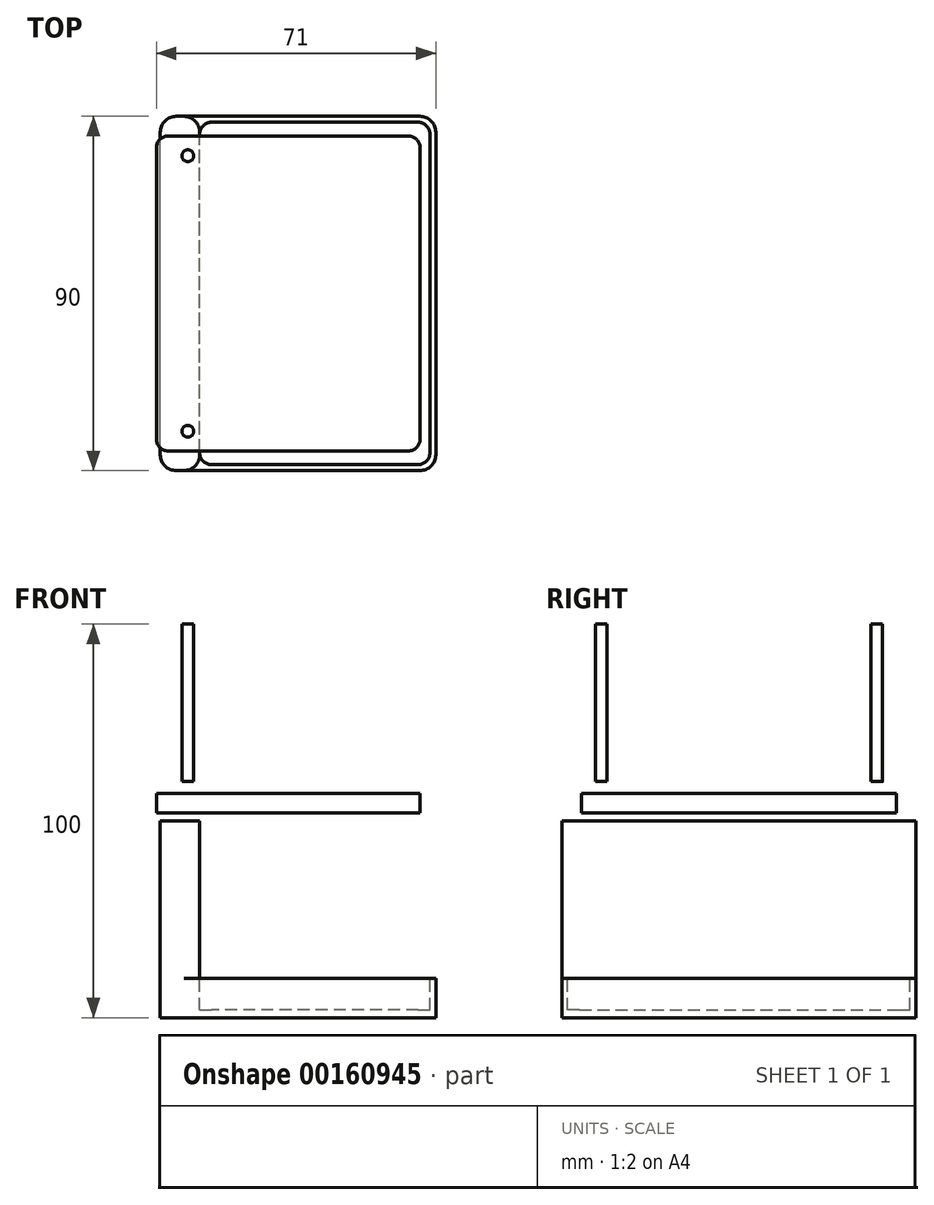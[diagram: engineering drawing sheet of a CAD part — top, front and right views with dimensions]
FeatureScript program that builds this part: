
annotation { "Feature Type Name" : "Feature", "Feature Type Description" : "" }
export const myFeature = defineFeature(function(context is Context, id is Id, definition is map)
    precondition{}
    {
        {
            var Q0;
            Q0=qCreatedBy(makeId("Front.planeOp"),FACE);
            var sketch = newSketch(context, id + "F0", { "sketchPlane" : qUnion([Q0])});
            skLineSegment(sketch, "E0", {"start": v(0, 0) * mm, "end": v(70, 0) * mm});
            skLineSegment(sketch, "E1", {"start": v(70, 0) * mm, "end": v(70, 10) * mm});
            skLineSegment(sketch, "E2", {"start": v(70, 10) * mm, "end": v(10, 10) * mm});
            skLineSegment(sketch, "E3", {"start": v(10, 10) * mm, "end": v(10, 50) * mm});
            skLineSegment(sketch, "E4", {"start": v(10, 50) * mm, "end": v(0, 50) * mm});
            skLineSegment(sketch, "E5", {"start": v(0, 50) * mm, "end": v(0, 0) * mm});
            skSolve(sketch);
        }
        {
            var Q0;
            Q0=makeQuery(id+"F0.imprint","IMPRINT",FACE,{"disambiguationData":[TD([[makeQuery(id+"F0.imprint","IMPRINT",EDGE,{"derivedFrom":sQuery(id+"F0.wireOp",EDGE,"E0")}),1.0]])]});
            extrude(context, id + "F1", {"entities" : qUnion([Q0]), "depth" : 45 * mm, "hasSecondDirection" : true, "secondDirectionOppositeDirection" : true, "secondDirectionDepth" : 45 * mm});
        }
        {
            var Q0;
            Q0=makeQuery(id+"F1.opExtrude","SWEPT_FACE",FACE,{"disambiguationData":[OSD([sQuery(id+"F0.wireOp",EDGE,"E4")])]});
            cPlane(context, id + "F2", {"entities" : qUnion([Q0]), "cplaneType" : CPlaneType.OFFSET, "offset" : 10 * mm, "width" : 150 * mm, "height" : 150 * mm});
        }
        {
            var Q0;
            Q0=qCreatedBy(makeId("Front.planeOp"),FACE);
            var sketch = newSketch(context, id + "F3", { "sketchPlane" : qUnion([Q0])});
            skLineSegment(sketch, "E6.bottom", {"start": v(-1, 57) * mm, "end": v(66, 57) * mm});
            skLineSegment(sketch, "E6.top", {"start": v(-1, 52) * mm, "end": v(66, 52) * mm});
            skLineSegment(sketch, "E6.left", {"start": v(-1, 57) * mm, "end": v(-1, 52) * mm});
            skLineSegment(sketch, "E6.right", {"start": v(66, 57) * mm, "end": v(66, 52) * mm});
            skSolve(sketch);
        }
        {
            var Q0;
            Q0=makeQuery(id+"F1.opExtrude","SWEPT_FACE",FACE,{"disambiguationData":[OSD([sQuery(id+"F0.wireOp",EDGE,"E2")])]});
            var sketch = newSketch(context, id + "F4", { "sketchPlane" : qUnion([Q0])});
            skLineSegment(sketch, "E7.bottom", {"start": v(65.5, 43.5) * mm, "end": v(13, 43.5) * mm});
            skLineSegment(sketch, "E7.top", {"start": v(65.5, -43.5) * mm, "end": v(13, -43.5) * mm});
            skLineSegment(sketch, "E7.left", {"start": v(68.5, 40.5) * mm, "end": v(68.5, -40.5) * mm});
            skLineSegment(sketch, "E7.right", {"start": v(10, 40.5) * mm, "end": v(10, -40.5) * mm});
            skPoint(sketch, "E8.visualSharp", {"position": v(10, -43.5) * mm});
            skArc(sketch, "E8.filletArc", {"start": v(10, -40.5) * mm, "mid": v(10.88, -42.62) * mm, "end": v(13, -43.5) * mm});
            skPoint(sketch, "E9.visualSharp", {"position": v(10, 43.5) * mm});
            skArc(sketch, "E9.filletArc", {"start": v(13, 43.5) * mm, "mid": v(10.88, 42.62) * mm, "end": v(10, 40.5) * mm});
            skPoint(sketch, "E10.visualSharp", {"position": v(68.5, -43.5) * mm});
            skArc(sketch, "E10.filletArc", {"start": v(65.5, -43.5) * mm, "mid": v(67.62, -42.62) * mm, "end": v(68.5, -40.5) * mm});
            skPoint(sketch, "E11.visualSharp", {"position": v(68.5, 43.5) * mm});
            skArc(sketch, "E11.filletArc", {"start": v(68.5, 40.5) * mm, "mid": v(67.62, 42.62) * mm, "end": v(65.5, 43.5) * mm});
            skSolve(sketch);
        }
        {
            var Q0;
            Q0=makeQuery(id+"F4.imprint","IMPRINT",FACE,{"disambiguationData":[TD([[makeQuery(id+"F4.imprint","IMPRINT",EDGE,{"derivedFrom":sQuery(id+"F4.wireOp",EDGE,"E7.bottom")}),1.0]])]});
            extrude(context, id + "F5", {"entities" : qUnion([Q0]), "operationType" : NewBodyOperationType.REMOVE, "oppositeDirection" : true, "depth" : 8 * mm});
        }
        {
            var Q0;
            Q0 = qSketchRegion(id + "F3", true);
            extrude(context, id + "F6", {"entities" : qUnion([Q0]), "operationType" : NewBodyOperationType.ADD, "oppositeDirection" : true, "depth" : 40 * mm, "hasSecondDirection" : true, "secondDirectionOppositeDirection" : false, "secondDirectionDepth" : 40 * mm});
        }
        {
            var Q0;
            Q0=makeQuery(id+"F1.opExtrude","CAP_EDGE",EDGE,{"disambiguationData":[OSD([sQuery(id+"F0.wireOp",EDGE,"E1")])],"isStart":false});
            var Q1;
            Q1=makeQuery(id+"F1.opExtrude","CAP_EDGE",EDGE,{"disambiguationData":[OSD([sQuery(id+"F0.wireOp",EDGE,"E1")])],"isStart":true});
            var Q2;
            Q2=makeQuery(id+"F1.opExtrude","CAP_EDGE",EDGE,{"disambiguationData":[OSD([sQuery(id+"F0.wireOp",EDGE,"E5")])],"isStart":false});
            var Q3;
            Q3=makeQuery(id+"F1.opExtrude","CAP_EDGE",EDGE,{"disambiguationData":[OSD([sQuery(id+"F0.wireOp",EDGE,"E5")])],"isStart":true});
            var Q4;
            Q4=makeQuery(id+"F1.opExtrude","CAP_EDGE",EDGE,{"disambiguationData":[OSD([sQuery(id+"F0.wireOp",EDGE,"E3")])],"isStart":false});
            var Q5;
            Q5=makeQuery(id+"F1.opExtrude","CAP_EDGE",EDGE,{"disambiguationData":[OSD([sQuery(id+"F0.wireOp",EDGE,"E3")])],"isStart":true});
            fillet(context, id + "F7", {"entities" : qUnion([Q0, Q1, Q2, Q3, Q4, Q5]), "radius" : 4 * mm, "tangentPropagation" : true, "allowEdgeOverflow" : false});
        }
        {
            var Q0;
            Q0=makeQuery(id+"F6.opExtrude","CAP_EDGE",EDGE,{"disambiguationData":[OSD([sQuery(id+"F3.wireOp",EDGE,"E6.right")])],"isStart":true});
            var Q1;
            Q1=makeQuery(id+"F6.opExtrude","CAP_EDGE",EDGE,{"disambiguationData":[OSD([sQuery(id+"F3.wireOp",EDGE,"E6.right")])],"isStart":false});
            var Q2;
            Q2=makeQuery(id+"F6.opExtrude","CAP_EDGE",EDGE,{"disambiguationData":[OSD([sQuery(id+"F3.wireOp",EDGE,"E6.left")])],"isStart":false});
            var Q3;
            Q3=makeQuery(id+"F6.opExtrude","CAP_EDGE",EDGE,{"disambiguationData":[OSD([sQuery(id+"F3.wireOp",EDGE,"E6.left")])],"isStart":true});
            fillet(context, id + "F8", {"entities" : qUnion([Q0, Q1, Q2, Q3]), "radius" : 3 * mm, "tangentPropagation" : true, "allowEdgeOverflow" : false});
        }
        {
            var Q0;
            Q0=qCreatedBy(id+"F2.planeOp",FACE);
            var sketch = newSketch(context, id + "F9", { "sketchPlane" : qUnion([Q0])});
            skCircle(sketch, "E12", {"center": v(7, -35) * mm, "radius": 1.5 * mm});
            skCircle(sketch, "E13", {"center": v(7, 35) * mm, "radius": 1.5 * mm});
            skSolve(sketch);
        }
        {
            var Q0;
            Q0 = qSketchRegion(id + "F9", true);
            extrude(context, id + "F10", {"entities" : qUnion([Q0]), "operationType" : NewBodyOperationType.ADD, "depth" : 40 * mm});
        }
    });
